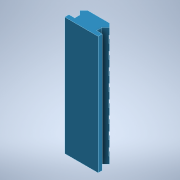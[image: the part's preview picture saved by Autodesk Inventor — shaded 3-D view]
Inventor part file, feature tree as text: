
AUTODESK INVENTOR PART (.ipt)
format: ipt  version: 2022 (Build 260153000, 153)  size: 440,320 bytes
history: native  units: mm
features: extrude x2, sketch x2, other x1, pattern_linear x1
ambient origin geometry x8: Origin, YZ Plane, XZ Plane, XY Plane, X Axis, Y Axis, Z Axis, Center Point
bodies: Body1 (feature_tree)
feature tree (6):
  other  "Твердое тело1"
  extrude  "Выдавливание1"  Depth=21.209mm
  extrude  "Выдавливание2"  Depth=9.3218mm
  pattern_linear  "Прямоуг.массив1"  Spacing1=15.6718mm  [1 undecoded]
  sketch  "Эскиз1"
  sketch  "Эскиз2"
note: 1 required parameter value undecoded (feature->parameter linkage not recoverable at this tier; creation-order binding heuristic only, values carry confidence <= 0.55)
